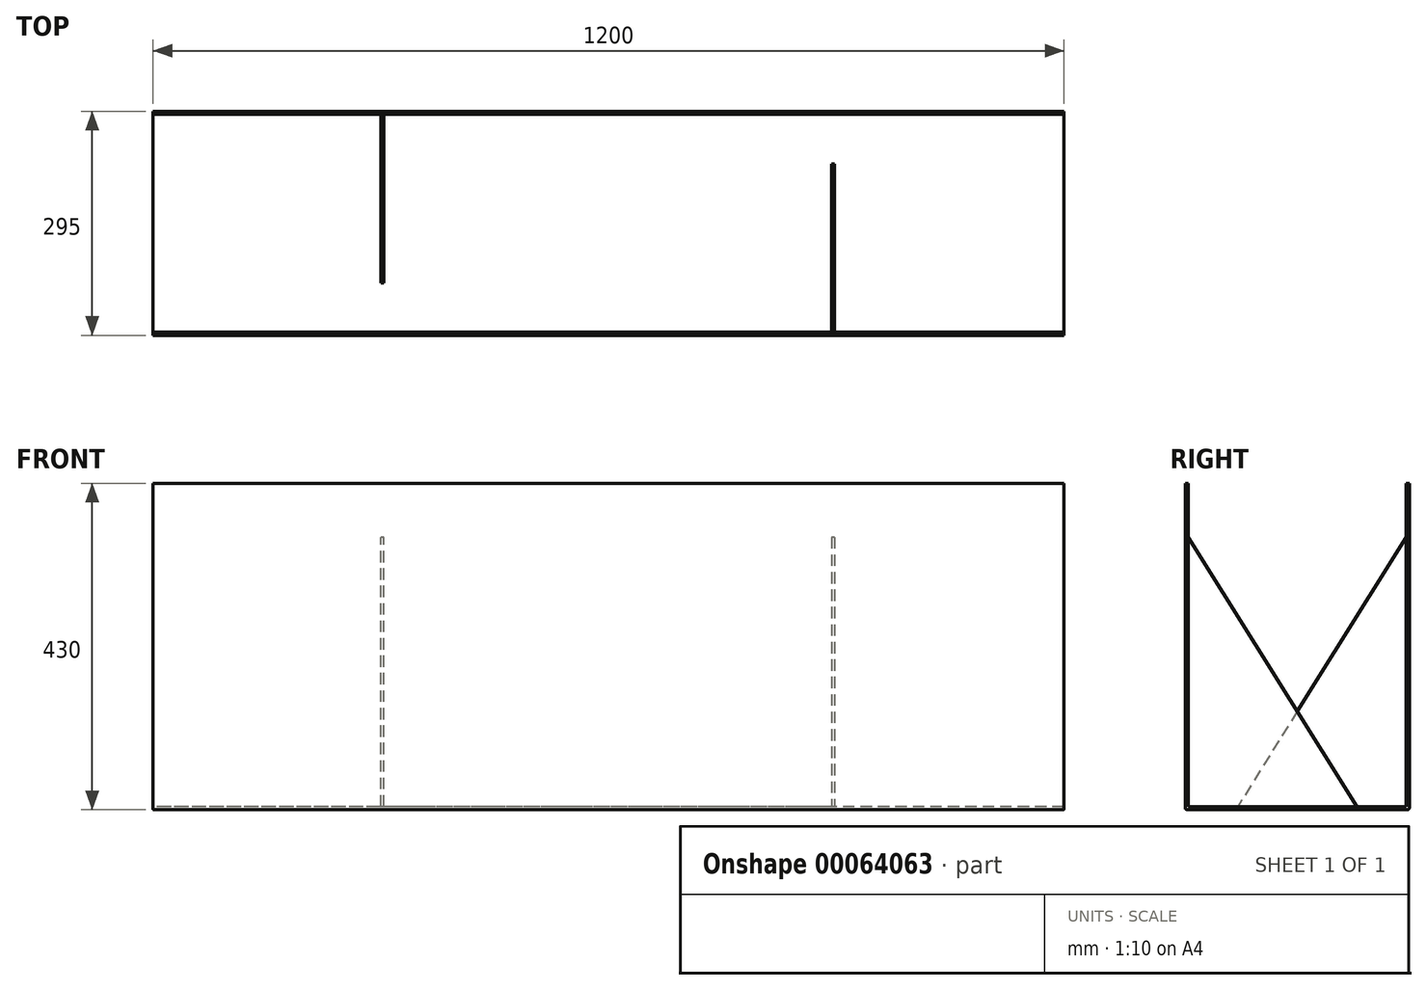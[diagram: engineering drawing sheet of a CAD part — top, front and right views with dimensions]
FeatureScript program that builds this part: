
annotation { "Feature Type Name" : "Feature", "Feature Type Description" : "" }
export const myFeature = defineFeature(function(context is Context, id is Id, definition is map)
    precondition{}
    {
        {
            var Q0;
            Q0=qCreatedBy(makeId("Right.planeOp"),FACE);
            var sketch = newSketch(context, id + "F0", { "sketchPlane" : qUnion([Q0])});
            skLineSegment(sketch, "E0.left", {"start": v(0, 0) * mm, "end": v(0, 430) * mm});
            skLineSegment(sketch, "E1", {"start": v(0, 0) * mm, "end": v(-295, 0) * mm});
            skLineSegment(sketch, "E2", {"start": v(-295, 0) * mm, "end": v(-295, 430) * mm});
            skLineSegment(sketch, "E3.0", {"start": v(-291, 4) * mm, "end": v(-291, 430) * mm});
            skLineSegment(sketch, "E3.1", {"start": v(-4, 4) * mm, "end": v(-291, 4) * mm});
            skLineSegment(sketch, "E3.2", {"start": v(-4, 4) * mm, "end": v(-4, 430) * mm});
            skLineSegment(sketch, "E4", {"start": v(0, 430) * mm, "end": v(-4, 430) * mm});
            skLineSegment(sketch, "E5", {"start": v(-291, 430) * mm, "end": v(-295, 430) * mm});
            skSolve(sketch);
        }
        {
            var Q0;
            Q0=makeQuery(id+"F0.imprint","IMPRINT",FACE,{"disambiguationData":[TD([[makeQuery(id+"F0.imprint","IMPRINT",EDGE,{"derivedFrom":sQuery(id+"F0.wireOp",EDGE,"E0.bottom")}),-1.0]])]});
            var Q1;
            Q1=makeQuery(id+"F0.imprint","IMPRINT",FACE,{"disambiguationData":[TD([[makeQuery(id+"F0.imprint","IMPRINT",EDGE,{"derivedFrom":sQuery(id+"F0.wireOp",EDGE,"E0.left")}),1.0]])]});
            extrude(context, id + "F1", {"entities" : qUnion([Q0, Q1]), "depth" : 1200 * mm});
        }
        {
            var Q0;
            Q0=qCreatedBy(makeId("Right.planeOp"),FACE);
            cPlane(context, id + "F2", {"entities" : qUnion([Q0]), "cplaneType" : CPlaneType.OFFSET, "offset" : 300 * mm, "width" : 150 * mm, "height" : 150 * mm});
        }
        {
            var Q0;
            Q0=qCreatedBy(id+"F2.planeOp",FACE);
            var sketch = newSketch(context, id + "F3", { "sketchPlane" : qUnion([Q0])});
            skLineSegment(sketch, "E6.0", {"start": v(-4, 4) * mm, "end": v(-4, 359) * mm});
            skLineSegment(sketch, "E7.0", {"start": v(-4, 4) * mm, "end": v(-226, 4) * mm});
            skPoint(sketch, "E8", {"position": v(-226, 4) * mm});
            skPoint(sketch, "E9", {"position": v(-4, 359) * mm});
            skLineSegment(sketch, "E10", {"start": v(-4, 359) * mm, "end": v(-226, 4) * mm});
            skSolve(sketch);
        }
        {
            var Q0;
            Q0=makeQuery(id+"F3.imprint","IMPRINT",FACE,{"disambiguationData":[TD([[makeQuery(id+"F3.imprint","IMPRINT",EDGE,{"derivedFrom":sQuery(id+"F3.wireOp",EDGE,"E6.0")}),1.0]])]});
            extrude(context, id + "F4", {"entities" : qUnion([Q0]), "depth" : 4 * mm});
        }
        {
            var Q0;
            Q0=makeQuery(id+"F4.opExtrude","CAP_FACE",FACE,{"disambiguationData":[OSD([sQuery(id+"F3.wireOp",EDGE,"E6.0"),sQuery(id+"F3.wireOp",EDGE,"E7.0"),sQuery(id+"F3.wireOp",EDGE,"E10")])],"isStart":false});
            cPlane(context, id + "F5", {"entities" : qUnion([Q0]), "cplaneType" : CPlaneType.OFFSET, "offset" : 590 * mm, "width" : 150 * mm, "height" : 150 * mm});
        }
        {
            var Q0;
            Q0=qCreatedBy(id+"F5.planeOp",FACE);
            var sketch = newSketch(context, id + "F6", { "sketchPlane" : qUnion([Q0])});
            skLineSegment(sketch, "E11", {"start": v(-291, 4) * mm, "end": v(-69, 4) * mm});
            skLineSegment(sketch, "E12", {"start": v(-69, 4) * mm, "end": v(-291, 359) * mm});
            skLineSegment(sketch, "E13", {"start": v(-291, 359) * mm, "end": v(-291, 4) * mm});
            skSolve(sketch);
        }
        {
            var Q0;
            Q0=makeQuery(id+"F6.imprint","IMPRINT",FACE,{"disambiguationData":[TD([[makeQuery(id+"F6.imprint","IMPRINT",EDGE,{"derivedFrom":sQuery(id+"F6.wireOp",EDGE,"E11")}),1.0]])]});
            extrude(context, id + "F7", {"entities" : qUnion([Q0]), "operationType" : NewBodyOperationType.ADD, "depth" : 4 * mm});
        }
        {
            var Q0;
            Q0=qCreatedBy(makeId("Top.planeOp"),FACE);
            var sketch = newSketch(context, id + "F8", { "sketchPlane" : qUnion([Q0])});
            skLineSegment(sketch, "E14.bottom", {"start": v(0, 0) * mm, "end": v(1200, 0) * mm});
            skLineSegment(sketch, "E14.top", {"start": v(0, -230) * mm, "end": v(1200, -230) * mm});
            skLineSegment(sketch, "E14.left", {"start": v(0, 0) * mm, "end": v(0, -230) * mm});
            skLineSegment(sketch, "E14.right", {"start": v(1200, 0) * mm, "end": v(1200, -230) * mm});
            skSolve(sketch);
        }
        {
            var Q0;
            Q0=makeQuery(id+"F8.imprint","IMPRINT",FACE,{"disambiguationData":[TD([[makeQuery(id+"F8.imprint","IMPRINT",EDGE,{"derivedFrom":sQuery(id+"F8.wireOp",EDGE,"E14.bottom")}),-1.0]])]});
            extrude(context, id + "F9", {"entities" : qUnion([Q0]), "operationType" : NewBodyOperationType.ADD, "depth" : 4 * mm});
        }
        {
            var Q0;
            Q0=makeQuery(id+"F1.opExtrude","SWEPT_EDGE",EDGE,{"disambiguationData":[OSD([sQuery(id+"F0.wireOp",EDGE,"E0.left"),sQuery(id+"F0.wireOp",EDGE,"E1")])]});
            var Q1;
            Q1=makeQuery(id+"F1.opExtrude","SWEPT_EDGE",EDGE,{"disambiguationData":[OSD([sQuery(id+"F0.wireOp",EDGE,"E1"),sQuery(id+"F0.wireOp",EDGE,"E2")])]});
            fillet(context, id + "F10", {"entities" : qUnion([Q0, Q1]), "radius" : 2 * mm, "tangentPropagation" : true, "allowEdgeOverflow" : false});
        }
    });
